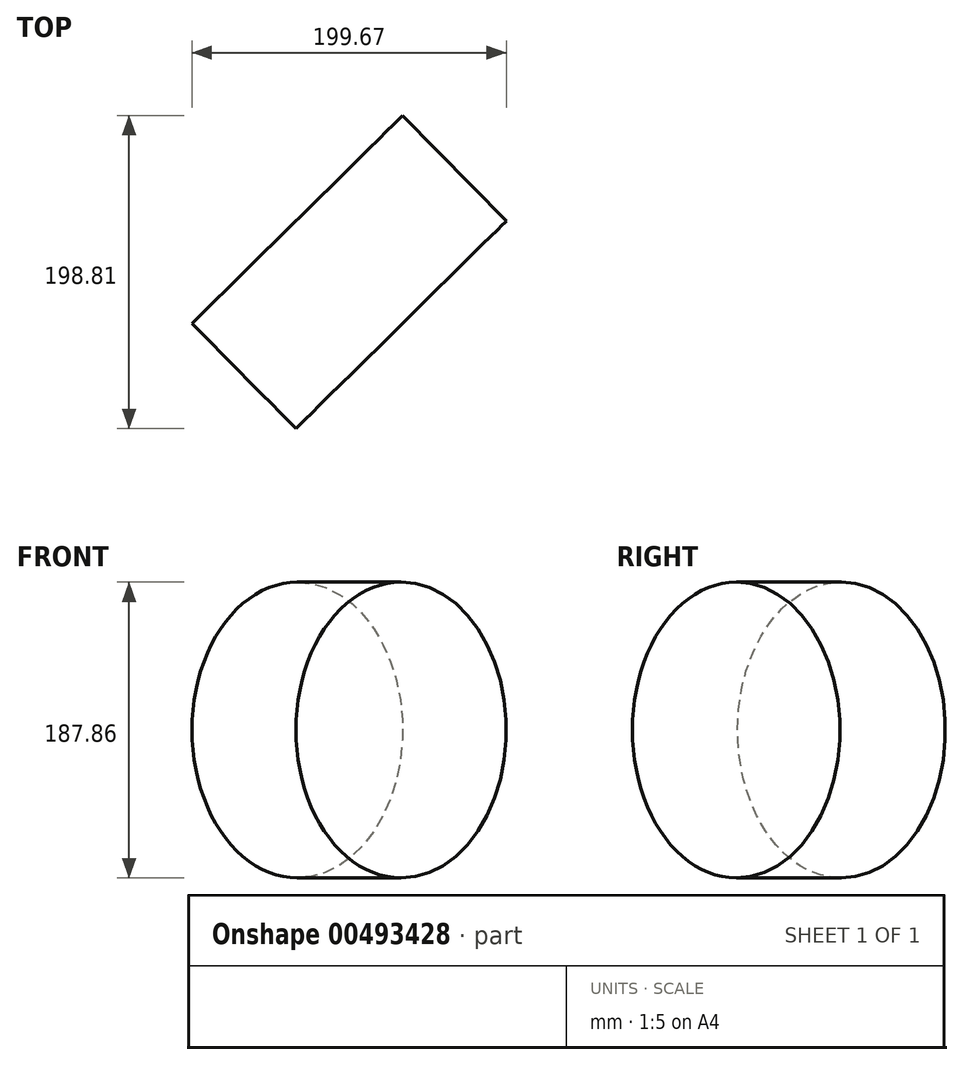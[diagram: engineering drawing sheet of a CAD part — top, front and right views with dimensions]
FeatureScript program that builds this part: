
annotation { "Feature Type Name" : "Feature", "Feature Type Description" : "" }
export const myFeature = defineFeature(function(context is Context, id is Id, definition is map)
    precondition{}
    {
        {
            var Q0;
            Q0=qCreatedBy(makeId("Top.planeOp"),FACE);
            var sketch = newSketch(context, id + "F0", { "sketchPlane" : qUnion([Q0])});
            skCircle(sketch, "E0.cCircle", {"center": v(0, 0) * mm, "radius": 46.96 * mm, "construction": true});
            skLineSegment(sketch, "E0.0", {"start": v(66.41, -0.43) * mm, "end": v(-0.43, -66.41) * mm});
            skLineSegment(sketch, "E0.1", {"start": v(-0.43, -66.41) * mm, "end": v(-66.41, 0.43) * mm});
            skLineSegment(sketch, "E0.2", {"start": v(-66.41, 0.43) * mm, "end": v(0.43, 66.41) * mm});
            skLineSegment(sketch, "E0.3", {"start": v(0.43, 66.41) * mm, "end": v(66.41, -0.43) * mm});
            skPoint(sketch, "E0.0.midPoint", {"position": v(33, -33.42) * mm});
            skSolve(sketch);
        }
        {
            var Q0;
            Q0=makeQuery(id+"F0.imprint","IMPRINT",FACE,{"disambiguationData":[TD([[makeQuery(id+"F0.imprint","IMPRINT",EDGE,{"derivedFrom":sQuery(id+"F0.wireOp",EDGE,"E0.0")}),-1.0]])]});
            var Q1;
            Q1=sQuery(id+"F0.wireOp",EDGE,"E0.3");
            revolve(context, id + "F1", {"entities" : qUnion([Q0]), "axis" : qUnion([Q1]), "revolveType" : RevolveType.FULL});
        }
    });
